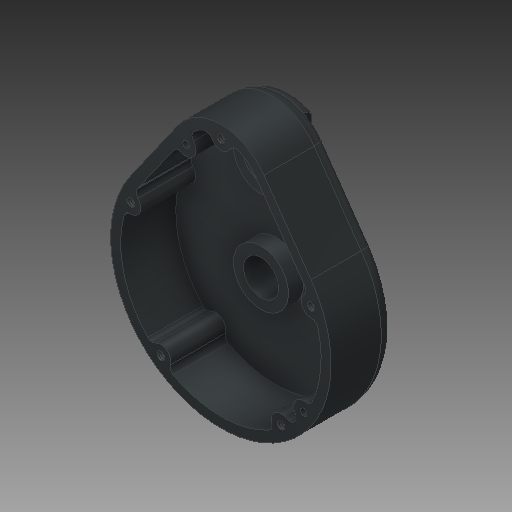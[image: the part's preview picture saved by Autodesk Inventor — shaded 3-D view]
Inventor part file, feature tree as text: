
AUTODESK INVENTOR PART (.ipt)
format: ipt  version: 2020 (Build 240168000, 168)  size: 518,656 bytes
history: native  units: in
note: dims shown in document units (in); Inventor stores cm internally (conversion verified against a paired STEP export)
features: extrude x4, revolve x4, sketch x4, hole x2, other x1, fillet x1
ambient origin geometry x8: Origin, YZ Plane, XZ Plane, XY Plane, X Axis, Y Axis, Z Axis, Center Point
bodies: Body1 (feature_tree)
feature tree (16):
  extrude  "Extrusion2"  Depth=1.3125in
  extrude  "Extrusion3"  Depth=2.5in
  extrude  "Extrusion4"  TaperAngle=0.0deg  [1 undecoded]
  extrude  "Extrusion5"  Depth=0.375in
  other  "Work Axis1"
  revolve  "Revolution1"  [1 undecoded]
  revolve  "Revolution2"  [1 undecoded]
  revolve  "Revolution3"  [1 undecoded]
  revolve  "Revolution4"  [1 undecoded]
  hole  "Hole1"  [1 undecoded]
  hole  "Hole2"  [1 undecoded]
  fillet  "Fillet1"  Radius=3.5in
  sketch  "Sketch1"  dims[d1=2.5in d2=1.0625in d21=1.3125in]
  sketch  "Sketch4"  dims[d23=2.75in d24=2.5in]
  sketch  "Sketch5"  dims[d25=0.875in d27=0.0in]
  sketch  "Sketch6"  dims[d28=1.625in d29=0.0in d30=2.5in d31=1.0625in d32=1.375in d33=0.0in d34=1.9375in d35=1.0in d36=2.25in d37=1.5in d38=2.937in d39=3.5in d40=0.0in d41=2.062in d42=1.375in d43=0.25in d44=2.5in d45=1.0625in d46=0.15in d47=0.1875in d48=1.375in d49=0.3765in d50=0.0in d51=0.1875in d52=0.196in d53=0.5in d54=0.375in d55=0.25in d56=0.5635in d57=0.625in d58=0.8108in d59=0.172in d60=0.5in d61=0.375in d62=0.25in d63=0.5635in d64=1.375in d65=0.8108in d66=1.125in d67=0.5625in d68=0.125in d69=0.0in d70=0.2812in d71=0.0312in d72=1.1811in d74=0.3125in d75=0.3937in d77=1.0in d79=3.813in d80=2.75in d81=0.0in d82=0.0in d83=2.625in d84=0.0in d85=180.0deg d87=2.625in d91=90.0deg d93=90.0deg d96=0.0625in d98=1.1875in d100=0.5625in d101=90.0deg d102=0.375in d103=0.25in d104=0.5625in d105=0.25in d106=0.25in d107=0.1275in d108=0.25in d109=0.125in d110=2.5in d111=0.1576in d112=1.0in d113=1.0in]
note: 7 required parameter values undecoded (feature->parameter linkage not recoverable at this tier; creation-order binding heuristic only, values carry confidence <= 0.55)